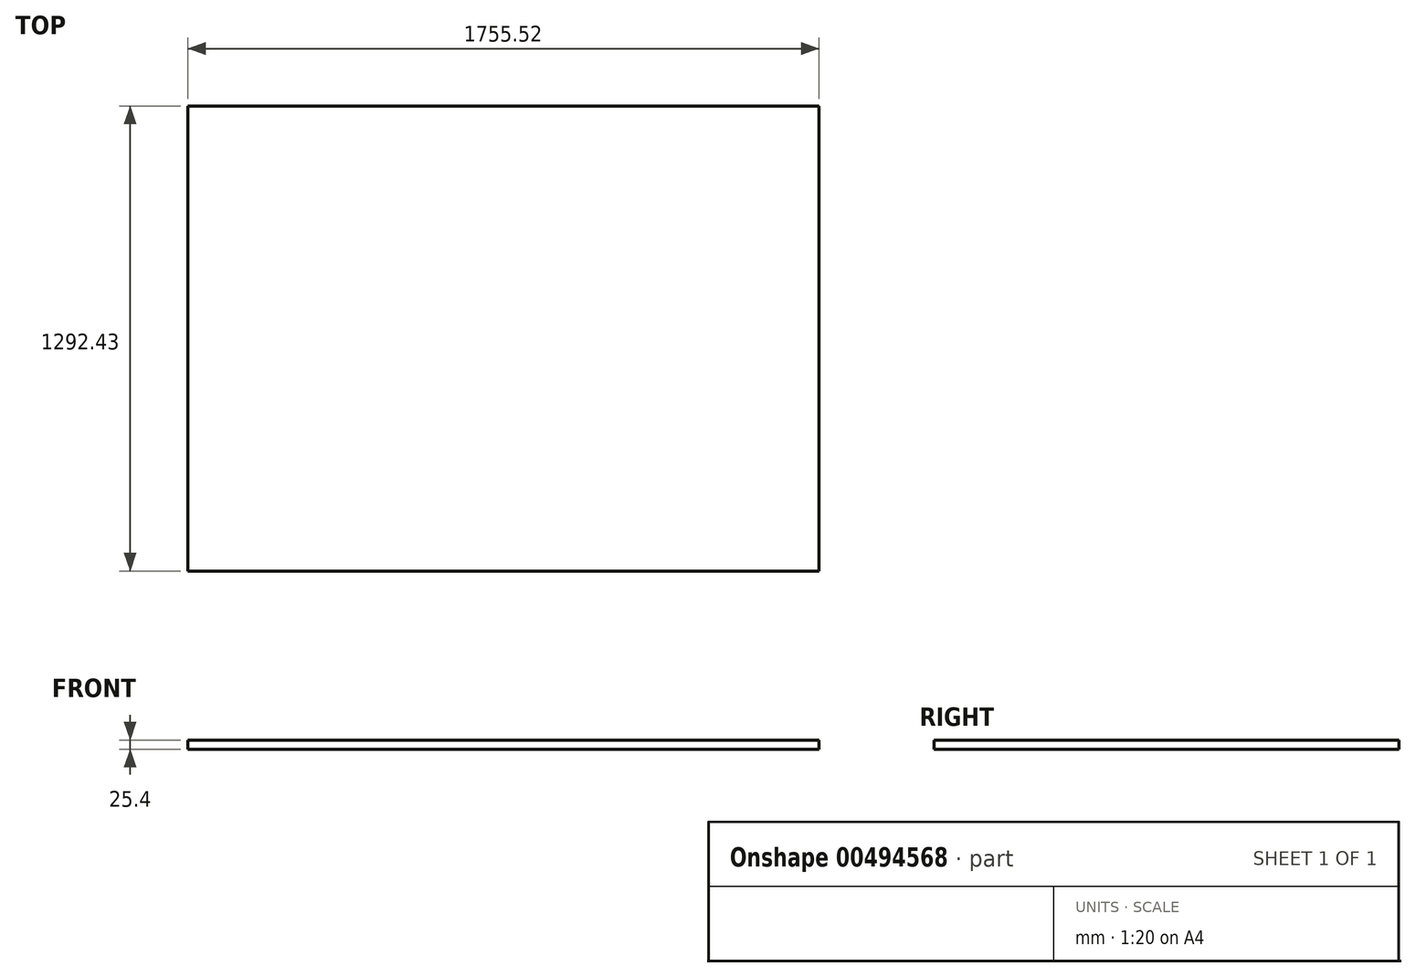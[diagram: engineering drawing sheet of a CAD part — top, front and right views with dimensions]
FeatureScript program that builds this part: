
annotation { "Feature Type Name" : "Feature", "Feature Type Description" : "" }
export const myFeature = defineFeature(function(context is Context, id is Id, definition is map)
    precondition{}
    {
        {
            var Q0;
            Q0=qCreatedBy(makeId("Top.planeOp"),FACE);
            var sketch = newSketch(context, id + "F0", { "sketchPlane" : qUnion([Q0])});
            skLineSegment(sketch, "E0.bottom", {"start": v(0, 0) * mm, "end": v(-1755.52, 0) * mm});
            skLineSegment(sketch, "E0.top", {"start": v(0, 1292.43) * mm, "end": v(-1755.52, 1292.43) * mm});
            skLineSegment(sketch, "E0.left", {"start": v(0, 0) * mm, "end": v(0, 1292.43) * mm});
            skLineSegment(sketch, "E0.right", {"start": v(-1755.52, 0) * mm, "end": v(-1755.52, 1292.43) * mm});
            skSolve(sketch);
        }
        {
            var Q0;
            Q0=makeQuery(id+"F0.imprint","IMPRINT",FACE,{"disambiguationData":[TD([[makeQuery(id+"F0.imprint","IMPRINT",EDGE,{"derivedFrom":sQuery(id+"F0.wireOp",EDGE,"E0.bottom")}),-1.0]])]});
            extrude(context, id + "F1", {"entities" : qUnion([Q0]), "depth" : 25.4 * mm});
        }
    });
